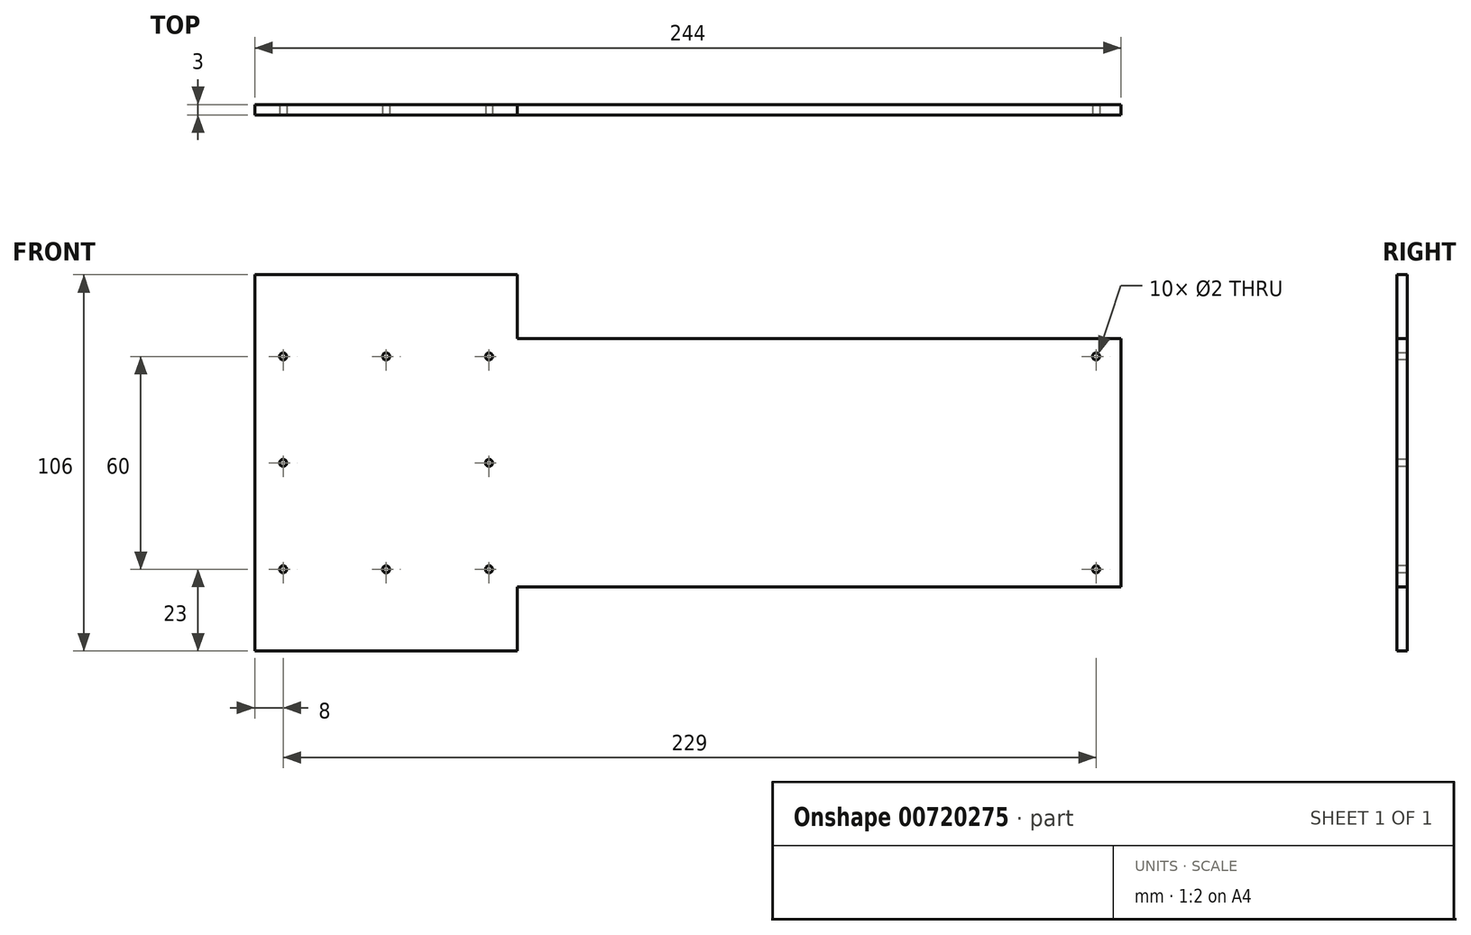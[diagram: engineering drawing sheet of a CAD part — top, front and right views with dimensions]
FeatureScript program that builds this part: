
annotation { "Feature Type Name" : "Feature", "Feature Type Description" : "" }
export const myFeature = defineFeature(function(context is Context, id is Id, definition is map)
    precondition{}
    {
        {
            var Q0;
            Q0=qCreatedBy(makeId("Front.planeOp"),FACE);
            var sketch = newSketch(context, id + "F0", { "sketchPlane" : qUnion([Q0])});
            skLineSegment(sketch, "E0.bottom", {"start": v(37, 53) * mm, "end": v(-37, 53) * mm});
            skLineSegment(sketch, "E0.top", {"start": v(37, -53) * mm, "end": v(-37, -53) * mm});
            skLineSegment(sketch, "E0.left", {"start": v(37, 53) * mm, "end": v(37, -53) * mm});
            skLineSegment(sketch, "E0.right", {"start": v(-37, 53) * mm, "end": v(-37, -53) * mm});
            skPoint(sketch, "E0.middle", {"position": v(0, 0) * mm});
            skPoint(sketch, "E1", {"position": v(-29, 0) * mm});
            skPoint(sketch, "E2", {"position": v(-29, 30) * mm});
            skPoint(sketch, "E3", {"position": v(29, 30) * mm});
            skPoint(sketch, "E4", {"position": v(29, 0) * mm});
            skPoint(sketch, "E5", {"position": v(29, -30) * mm});
            skPoint(sketch, "E6", {"position": v(-29, -30) * mm});
            skLineSegment(sketch, "E7.bottom", {"start": v(37, 0) * mm, "end": v(207, 0) * mm});
            skLineSegment(sketch, "E7.top", {"start": v(37, 35) * mm, "end": v(207, 35) * mm});
            skLineSegment(sketch, "E7.left", {"start": v(37, 0) * mm, "end": v(37, 35) * mm});
            skLineSegment(sketch, "E7.right", {"start": v(207, 0) * mm, "end": v(207, 35) * mm});
            skLineSegment(sketch, "E8.top", {"start": v(37, -35) * mm, "end": v(207, -35) * mm});
            skLineSegment(sketch, "E8.left", {"start": v(37, 0) * mm, "end": v(37, -35) * mm});
            skLineSegment(sketch, "E8.right", {"start": v(207, 0) * mm, "end": v(207, -35) * mm});
            skSolve(sketch);
        }
        {
            var Q0;
            Q0=makeQuery(id+"F0.imprint","IMPRINT",FACE,{"disambiguationData":[TD([[makeQuery(id+"F0.imprint","IMPRINT",EDGE,{"derivedFrom":sQuery(id+"F0.wireOp",EDGE,"E0.bottom")}),1.0]])]});
            var Q1;
            Q1=makeQuery(id+"F0.imprint","IMPRINT",FACE,{"disambiguationData":[TD([[makeQuery(id+"F0.imprint","IMPRINT",EDGE,{"derivedFrom":sQuery(id+"F0.wireOp",EDGE,"E7.bottom")}),-1.0]])]});
            var Q2;
            Q2=makeQuery(id+"F0.imprint","IMPRINT",FACE,{"disambiguationData":[TD([[makeQuery(id+"F0.imprint","IMPRINT",EDGE,{"derivedFrom":sQuery(id+"F0.wireOp",EDGE,"E7.top")}),-1.0]])]});
            extrude(context, id + "F1", {"entities" : qUnion([Q0, Q1, Q2]), "depth" : 3 * mm, "offsetDistance" : 25 * mm});
        }
        {
            var Q0;
            Q0=sQuery(id+"F0.wireOp",VERTEX,"E1");
            var Q1;
            Q1=sQuery(id+"F0.wireOp",VERTEX,"E4");
            var Q2;
            Q2=makeQuery(id+"F1.opExtrude","SWEPT_BODY",BODY,{"disambiguationData":[OSD([sQuery(id+"F0.wireOp",EDGE,"E0.bottom"),sQuery(id+"F0.wireOp",EDGE,"E0.top"),sQuery(id+"F0.wireOp",EDGE,"E0.left"),sQuery(id+"F0.wireOp",EDGE,"E0.right")])]});
            hole(context, id + "F2", {"style" : HoleStyle.SIMPLE, "endStyle" : HoleEndStyle.BLIND, "oppositeDirection" : true, "holeDiameter" : 2 * mm, "majorDiameter" : 5 * mm, "holeDepth" : 40 * mm, "tappedDepth" : 12 * mm, "tapClearance" : 3, "locations" : qUnion([Q0, Q1]), "scope" : qUnion([Q2])});
        }
        {
            var Q0;
            Q0=sQuery(id+"F0.wireOp",VERTEX,"E5");
            var Q1;
            Q1=sQuery(id+"F0.wireOp",VERTEX,"E6");
            var Q2;
            Q2=sQuery(id+"F0.wireOp",VERTEX,"E3");
            var Q3;
            Q3=sQuery(id+"F0.wireOp",VERTEX,"E2");
            var Q4;
            Q4=makeQuery(id+"F1.opExtrude","SWEPT_BODY",BODY,{"disambiguationData":[OSD([sQuery(id+"F0.wireOp",EDGE,"E0.bottom"),sQuery(id+"F0.wireOp",EDGE,"E0.top"),sQuery(id+"F0.wireOp",EDGE,"E0.left"),sQuery(id+"F0.wireOp",EDGE,"E0.right")])]});
            hole(context, id + "F3", {"style" : HoleStyle.SIMPLE, "endStyle" : HoleEndStyle.BLIND, "oppositeDirection" : true, "holeDiameter" : 2 * mm, "majorDiameter" : 5 * mm, "holeDepth" : 40 * mm, "tappedDepth" : 12 * mm, "tapClearance" : 3, "locations" : qUnion([Q0, Q1, Q2, Q3]), "scope" : qUnion([Q4])});
        }
        {
            var Q0;
            Q0=makeQuery(id+"F0.imprint","IMPRINT",FACE,{"disambiguationData":[TD([[makeQuery(id+"F0.imprint","IMPRINT",EDGE,{"derivedFrom":sQuery(id+"F0.wireOp",EDGE,"E0.bottom")}),1.0]])]});
            var sketch = newSketch(context, id + "F4", { "sketchPlane" : qUnion([Q0])});
            skPoint(sketch, "E9", {"position": v(0, -30) * mm});
            skPoint(sketch, "E10", {"position": v(0, 30) * mm});
            skPoint(sketch, "E11", {"position": v(200, -30) * mm});
            skPoint(sketch, "E12", {"position": v(200, 30) * mm});
            skSolve(sketch);
        }
        {
            var Q0;
            Q0=sQuery(id+"F4.wireOp",VERTEX,"E9");
            var Q1;
            Q1=sQuery(id+"F4.wireOp",VERTEX,"E10");
            var Q2;
            Q2=sQuery(id+"F4.wireOp",VERTEX,"E11");
            var Q3;
            Q3=sQuery(id+"F4.wireOp",VERTEX,"E12");
            var Q4;
            Q4=makeQuery(id+"F1.opExtrude","SWEPT_BODY",BODY,{"disambiguationData":[OSD([sQuery(id+"F0.wireOp",EDGE,"E0.bottom"),sQuery(id+"F0.wireOp",EDGE,"E0.top"),sQuery(id+"F0.wireOp",EDGE,"E0.left"),sQuery(id+"F0.wireOp",EDGE,"E0.right")])]});
            hole(context, id + "F5", {"style" : HoleStyle.SIMPLE, "endStyle" : HoleEndStyle.BLIND, "oppositeDirection" : true, "holeDiameter" : 2 * mm, "majorDiameter" : 5 * mm, "holeDepth" : 40 * mm, "tappedDepth" : 12 * mm, "tapClearance" : 3, "locations" : qUnion([Q0, Q1, Q2, Q3]), "scope" : qUnion([Q4])});
        }
    });
